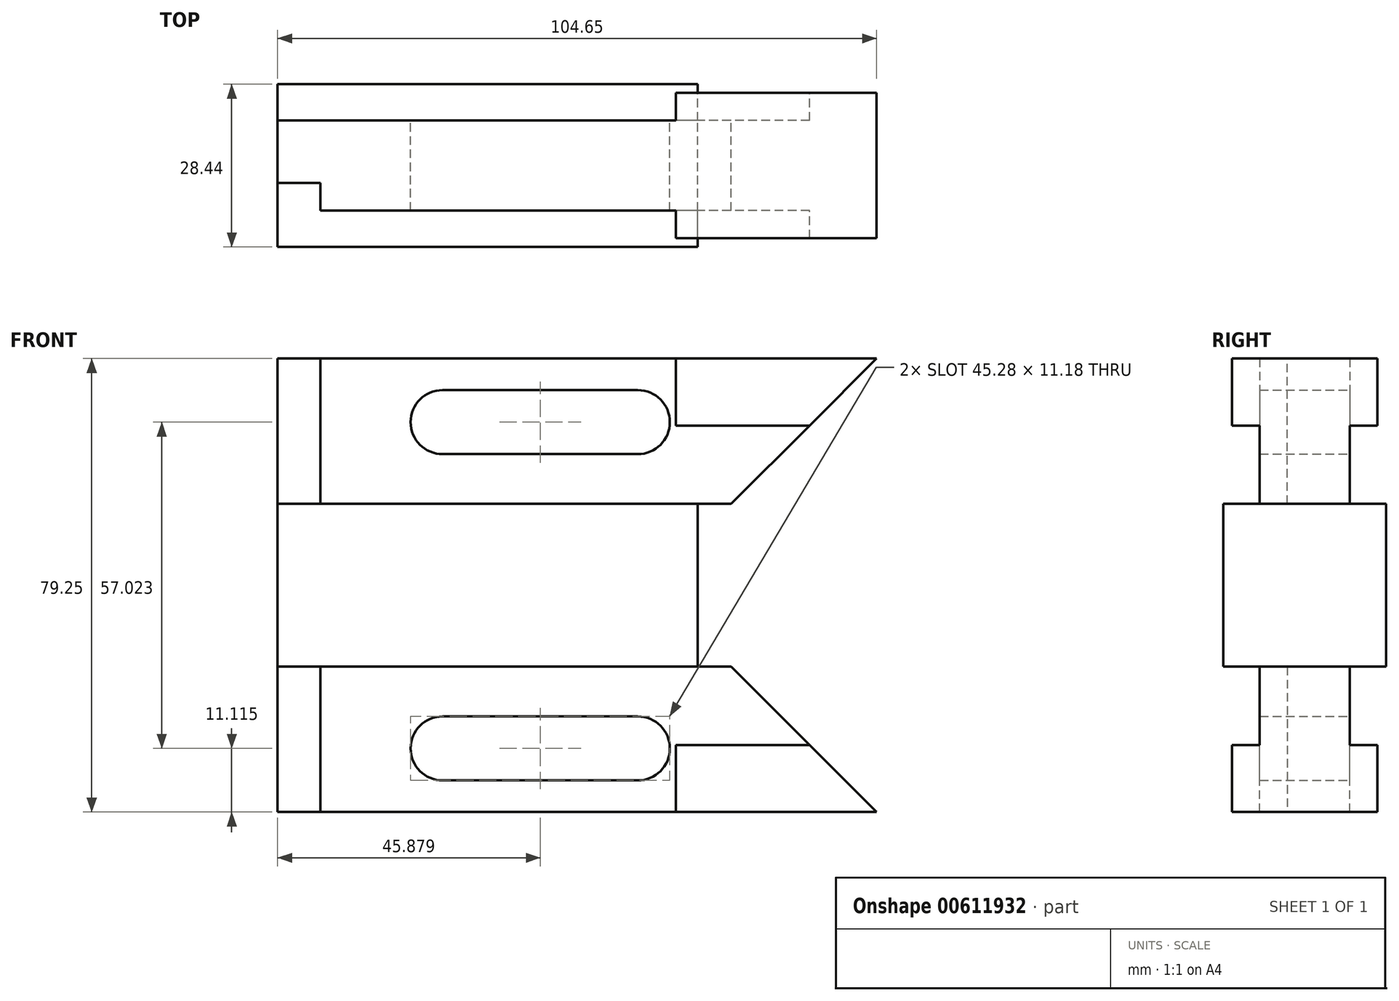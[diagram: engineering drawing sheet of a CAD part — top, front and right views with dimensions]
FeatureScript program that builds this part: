
annotation { "Feature Type Name" : "Feature", "Feature Type Description" : "" }
export const myFeature = defineFeature(function(context is Context, id is Id, definition is map)
    precondition{}
    {
        {
            var Q0;
            Q0=qCreatedBy(makeId("Front.planeOp"),FACE);
            var sketch = newSketch(context, id + "F0", { "sketchPlane" : qUnion([Q0])});
            skLineSegment(sketch, "E0.bottom", {"start": v(-25.4, 0) * mm, "end": v(-104.65, 0) * mm});
            skLineSegment(sketch, "E0.top", {"start": v(0, 25.4) * mm, "end": v(-104.65, 25.4) * mm});
            skLineSegment(sketch, "E0.right", {"start": v(-104.65, 0) * mm, "end": v(-104.65, 25.4) * mm});
            skLineSegment(sketch, "E1.bottom", {"start": v(-104.65, 0) * mm, "end": v(-31.24, 0) * mm});
            skLineSegment(sketch, "E1.top", {"start": v(-104.65, -14.22) * mm, "end": v(-31.24, -14.22) * mm});
            skLineSegment(sketch, "E1.left", {"start": v(-104.65, 0) * mm, "end": v(-104.65, -14.22) * mm});
            skLineSegment(sketch, "E1.right", {"start": v(-31.24, 0) * mm, "end": v(-31.24, -14.22) * mm});
            skLineSegment(sketch, "E2.bottom", {"start": v(-104.65, 25.4) * mm, "end": v(-97.18, 25.4) * mm});
            skLineSegment(sketch, "E2.top", {"start": v(-104.65, 0) * mm, "end": v(-97.18, 0) * mm});
            skLineSegment(sketch, "E2.left", {"start": v(-104.65, 25.4) * mm, "end": v(-104.65, 0) * mm});
            skLineSegment(sketch, "E3", {"start": v(0, 25.4) * mm, "end": v(-25.4, 0) * mm});
            skLineSegment(sketch, "E4.bottom", {"start": v(0, 25.4) * mm, "end": v(-35.05, 25.4) * mm});
            skLineSegment(sketch, "E4.top", {"start": v(-11.73, 13.67) * mm, "end": v(-35.05, 13.67) * mm});
            skLineSegment(sketch, "E4.right", {"start": v(-35.05, 25.4) * mm, "end": v(-35.05, 13.67) * mm});
            skLineSegment(sketch, "E5", {"start": v(-75.82, 25.49) * mm, "end": v(-75.82, 25.4) * mm});
            skPoint(sketch, "E6.third.point", {"position": v(-90.5, 25.4) * mm});
            skPoint(sketch, "E7.start.orphan", {"position": v(-75.82, 19.14) * mm});
            skArc(sketch, "E8", {"start": v(-75.82, 19.88) * mm, "mid": v(-81.41, 14.29) * mm, "end": v(-75.82, 8.7) * mm});
            skArc(sketch, "E9", {"start": v(-41.72, 8.7) * mm, "mid": v(-36.13, 14.29) * mm, "end": v(-41.72, 19.88) * mm});
            skLineSegment(sketch, "E10", {"start": v(-75.82, 19.88) * mm, "end": v(-41.72, 19.88) * mm});
            skLineSegment(sketch, "E11", {"start": v(-41.72, 8.7) * mm, "end": v(-75.82, 8.7) * mm});
            skLineSegment(sketch, "E12.trimOffspring", {"start": v(-75.82, 19.88) * mm, "end": v(-75.82, 19.14) * mm});
            skPoint(sketch, "E13.start.orphan", {"position": v(-75.82, -9.56) * mm});
            skLineSegment(sketch, "E14", {"start": v(-97.18, 25.4) * mm, "end": v(-97.18, 0) * mm});
            skLineSegment(sketch, "E15.trimOffspring", {"start": v(-75.82, 8.7) * mm, "end": v(-75.82, 7.96) * mm});
            skSolve(sketch);
        }
        {
            var Q0;
            Q0=makeQuery(id+"F0.imprint","IMPRINT",FACE,{"disambiguationData":[TD([[makeQuery(id+"F0.imprint","IMPRINT",EDGE,{"derivedFrom":sQuery(id+"F0.wireOp",EDGE,"E1.top")}),1.0]])]});
            extrude(context, id + "F1", {"entities" : qUnion([Q0]), "endBound" : BoundingType.SYMMETRIC, "depth" : 28.45 * mm, "offsetDistance" : 25.4 * mm});
        }
        {
            var Q0;
            {var subQ0=sQuery(id+"F0.wireOp",EDGE,"E4.top");Q0=makeQuery(id+"F0.imprint","IMPRINT",FACE,{"disambiguationData":[TD([[makeQuery(id+"F0.imprint","IMPRINT",EDGE,{"derivedFrom":subQ0}),1.0]])]});}
            extrude(context, id + "F2", {"entities" : qUnion([Q0]), "operationType" : NewBodyOperationType.ADD, "endBound" : BoundingType.SYMMETRIC, "depth" : 15.75 * mm, "offsetDistance" : 25.4 * mm});
        }
        {
            var Q0;
            {var subQ4=sQuery(id+"F0.wireOp",EDGE,"E4.top");Q0=makeQuery(id+"F0.imprint","IMPRINT",FACE,{"disambiguationData":[TD([[makeQuery(id+"F0.imprint","IMPRINT",EDGE,{"derivedFrom":subQ4}),-1.0]])]});}
            extrude(context, id + "F3", {"entities" : qUnion([Q0]), "operationType" : NewBodyOperationType.ADD, "endBound" : BoundingType.SYMMETRIC, "depth" : 25.4 * mm, "offsetDistance" : 25.4 * mm});
        }
        {
            var Q0;
            {var subQ0=sQuery(id+"F0.wireOp",EDGE,"E0.right");Q0=makeQuery(id+"F0.imprint","IMPRINT",FACE,{"disambiguationData":[TD([[makeQuery(id+"F0.imprint","IMPRINT",EDGE,{"derivedFrom":subQ0}),-1.0]])]});}
            extrude(context, id + "F4", {"entities" : qUnion([Q0]), "operationType" : NewBodyOperationType.ADD, "depth" : 3.05 * mm, "offsetDistance" : 25.4 * mm, "hasSecondDirection" : true, "secondDirectionOppositeDirection" : true, "secondDirectionDepth" : 7.87 * mm});
        }
        {
            var Q0;
            Q0=makeQuery(id+"F1.opExtrude","SWEPT_BODY",BODY,{"disambiguationData":[OSD([sQuery(id+"F0.wireOp",EDGE,"E0.bottom"),sQuery(id+"F0.wireOp",EDGE,"E1.top"),sQuery(id+"F0.wireOp",EDGE,"E1.left"),sQuery(id+"F0.wireOp",EDGE,"E1.right")])]});
            var Q1;
            Q1=makeQuery(id+"F1.opExtrude","SWEPT_FACE",FACE,{"disambiguationData":[OSD([sQuery(id+"F0.wireOp",EDGE,"E1.top")])]});
            mirror(context, id + "F5", {"operationType" : NewBodyOperationType.ADD, "entities" : qUnion([Q0]), "mirrorPlane" : qUnion([Q1])});
        }
    });
